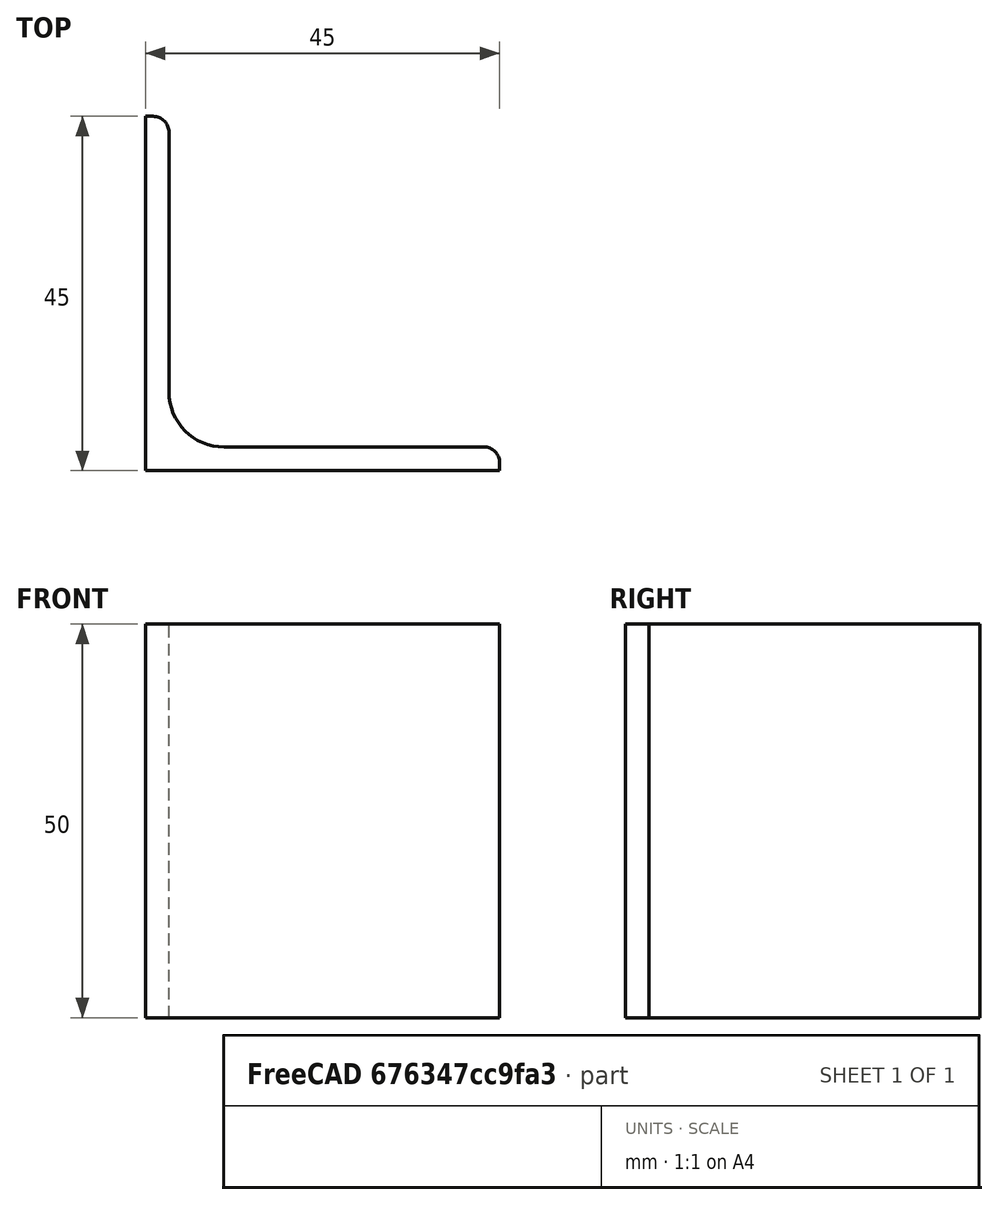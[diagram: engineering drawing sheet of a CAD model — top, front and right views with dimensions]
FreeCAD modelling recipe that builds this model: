
FCSTD DOCUMENT  (FreeCAD 0.15R4671 (Git))
Label: Angle Bar L45x45x3 EN10056 S235JR
License: All rights reserved
LicenseURL: http://en.wikipedia.org/wiki/All_rights_reserved
objects: Sketcher::SketchObject×1, Part::Extrusion×1
note: 2 computed .brp shape members not serialized (recipe doc carries the construction recipe); baked Part::Feature solids carry a one-line shape summary decoded from their .brp

FEATURE [Sketcher::SketchObject] Sketch
  sketch-geometry (9):
    g0: LineSegment StartX=0 StartY=0 StartZ=0 EndX=45 EndY=0 EndZ=0
    g1: LineSegment StartX=45 StartY=0 StartZ=0 EndX=45 EndY=1 EndZ=0
    g2: LineSegment StartX=43 StartY=3 StartZ=0 EndX=10 EndY=3 EndZ=0
    g3: LineSegment StartX=0 StartY=0 StartZ=0 EndX=0 EndY=45 EndZ=0
    g4: LineSegment StartX=0 StartY=45 StartZ=0 EndX=1 EndY=45 EndZ=0
    g5: LineSegment StartX=3 StartY=43 StartZ=0 EndX=3 EndY=10 EndZ=0
    g6: ArcOfCircle CenterX=10 CenterY=10 CenterZ=0 NormalX=0 NormalY=0 NormalZ=1 Radius=7 StartAngle=3.14159 EndAngle=4.71239
    g7: ArcOfCircle CenterX=1 CenterY=43 CenterZ=0 NormalX=0 NormalY=0 NormalZ=1 Radius=2 StartAngle=0 EndAngle=1.5708
    g8: ArcOfCircle CenterX=43 CenterY=1 CenterZ=0 NormalX=0 NormalY=0 NormalZ=1 Radius=2 StartAngle=0 EndAngle=1.5708
  constraints (23):
    c: Coincident(g0,g-1)
    c: Horizontal(g0)
    c: Coincident(g1,g0)
    c: Vertical(g1)
    c: Horizontal(g2)
    c: Coincident(g3,g-1)
    c: Vertical(g3)
    c: Coincident(g4,g3)
    c: Horizontal(g4)
    c: Vertical(g5)
    c: Tangent(g5,g6) = -1.5708
    c: Tangent(g2,g6) = 1.5708
    c: Tangent(g4,g7) = 1.5708
    c: Tangent(g5,g7) = 1.5708
    c: Tangent(g2,g8) = -1.5708
    c: Tangent(g1,g8) = -1.5708
    c: DistanceX(g0) = 45
    c: DistanceY(g3) = 45
    c: DistanceY(g0,g2) = 3
    c: DistanceX(g3,g5) = 3
    c: Radius(g6) = 7
    c: Radius(g8) = 2
    c: Radius(g7) = 2
FEATURE [Part::Extrusion] Extrude  label="Angle Bar L45x45x3 EN10056 S235JR"
  Base = -> Sketch
  Dir = (0,0,50)
  Solid = true
